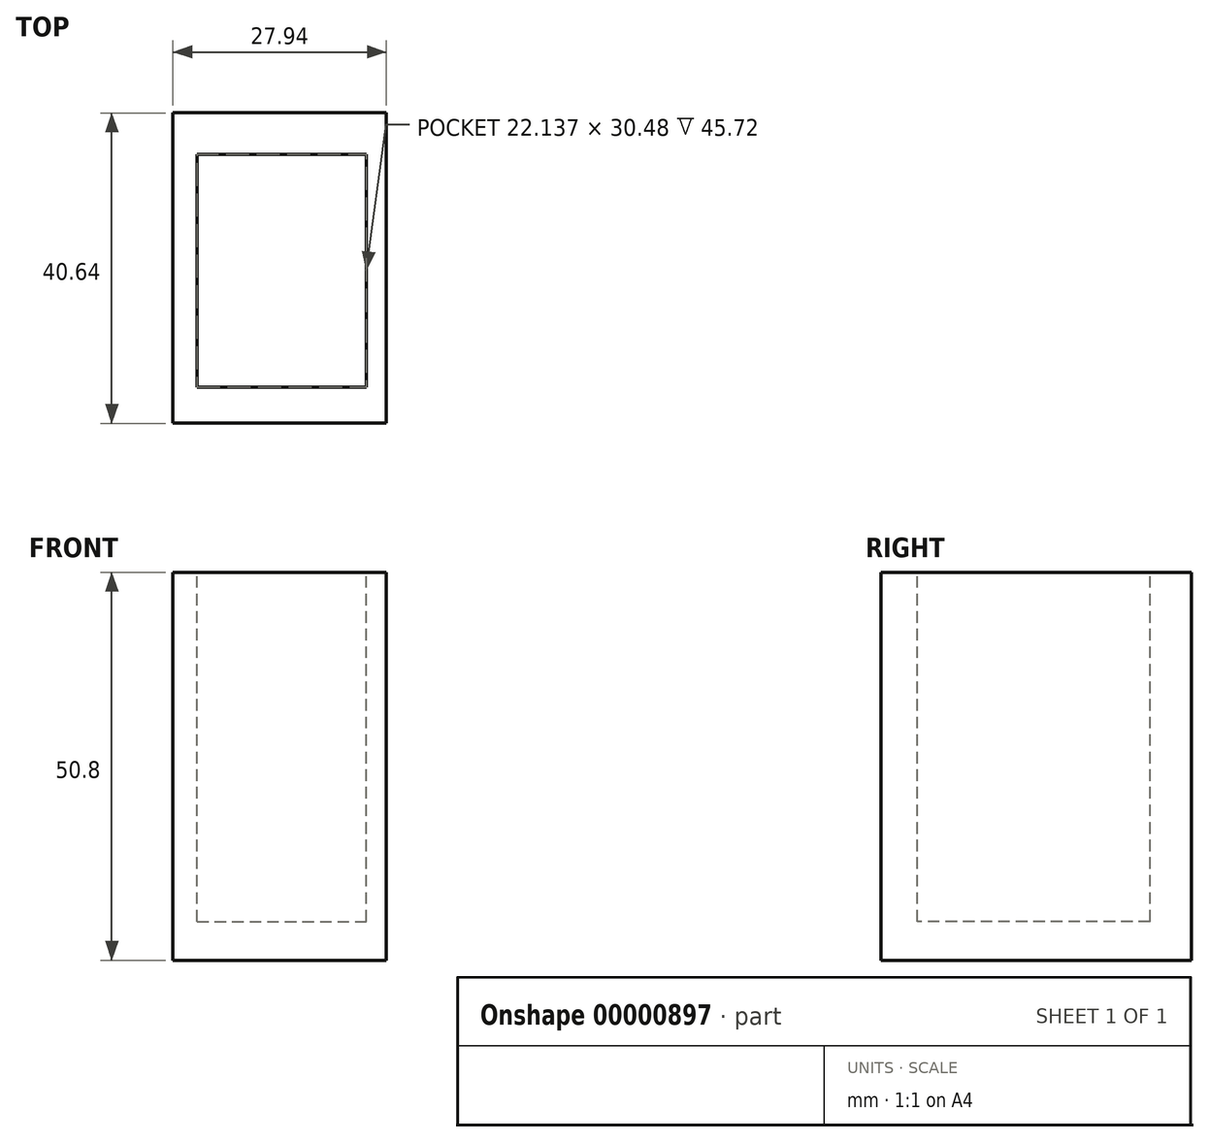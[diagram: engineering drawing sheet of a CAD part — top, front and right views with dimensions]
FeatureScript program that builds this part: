
annotation { "Feature Type Name" : "Feature", "Feature Type Description" : "" }
export const myFeature = defineFeature(function(context is Context, id is Id, definition is map)
    precondition{}
    {
        {
            var Q0;
            Q0=qCreatedBy(makeId("Top.planeOp"),FACE);
            var sketch = newSketch(context, id + "F0", { "sketchPlane" : qUnion([Q0])});
            skLineSegment(sketch, "E0.bottom", {"start": v(-23.06, 17.11) * mm, "end": v(4.88, 17.11) * mm});
            skLineSegment(sketch, "E0.top", {"start": v(-23.06, -23.53) * mm, "end": v(4.88, -23.53) * mm});
            skLineSegment(sketch, "E0.left", {"start": v(-23.06, 17.11) * mm, "end": v(-23.06, -23.53) * mm});
            skLineSegment(sketch, "E0.right", {"start": v(4.88, 17.11) * mm, "end": v(4.88, -23.53) * mm});
            skSolve(sketch);
        }
        {
            var Q0;
            Q0=makeQuery(id+"F0.imprint","IMPRINT",FACE,{"disambiguationData":[TD([[makeQuery(id+"F0.imprint","IMPRINT",EDGE,{"derivedFrom":sQuery(id+"F0.wireOp",EDGE,"E0.bottom")}),-1.0]])]});
            extrude(context, id + "F1", {"entities" : qUnion([Q0]), "depth" : 50.8 * mm});
        }
        {
            var Q0;
            Q0=makeQuery(id+"F1.opExtrude","CAP_FACE",FACE,{"disambiguationData":[OSD([sQuery(id+"F0.wireOp",EDGE,"E0.bottom"),sQuery(id+"F0.wireOp",EDGE,"E0.top"),sQuery(id+"F0.wireOp",EDGE,"E0.left"),sQuery(id+"F0.wireOp",EDGE,"E0.right")])],"isStart":false});
            var sketch = newSketch(context, id + "F2", { "sketchPlane" : qUnion([Q0])});
            skLineSegment(sketch, "E1.bottom", {"start": v(-19.9, 11.71) * mm, "end": v(2.23, 11.71) * mm});
            skLineSegment(sketch, "E1.top", {"start": v(-19.9, -18.77) * mm, "end": v(2.23, -18.77) * mm});
            skLineSegment(sketch, "E1.left", {"start": v(-19.9, 11.71) * mm, "end": v(-19.9, -18.77) * mm});
            skLineSegment(sketch, "E1.right", {"start": v(2.23, 11.71) * mm, "end": v(2.23, -18.77) * mm});
            skSolve(sketch);
        }
        {
            var Q0;
            Q0=makeQuery(id+"F2.imprint","IMPRINT",FACE,{"disambiguationData":[TD([[makeQuery(id+"F2.imprint","IMPRINT",EDGE,{"derivedFrom":sQuery(id+"F2.wireOp",EDGE,"E1.bottom")}),-1.0]])]});
            extrude(context, id + "F3", {"entities" : qUnion([Q0]), "operationType" : NewBodyOperationType.REMOVE, "oppositeDirection" : true, "depth" : 45.72 * mm});
        }
    });
